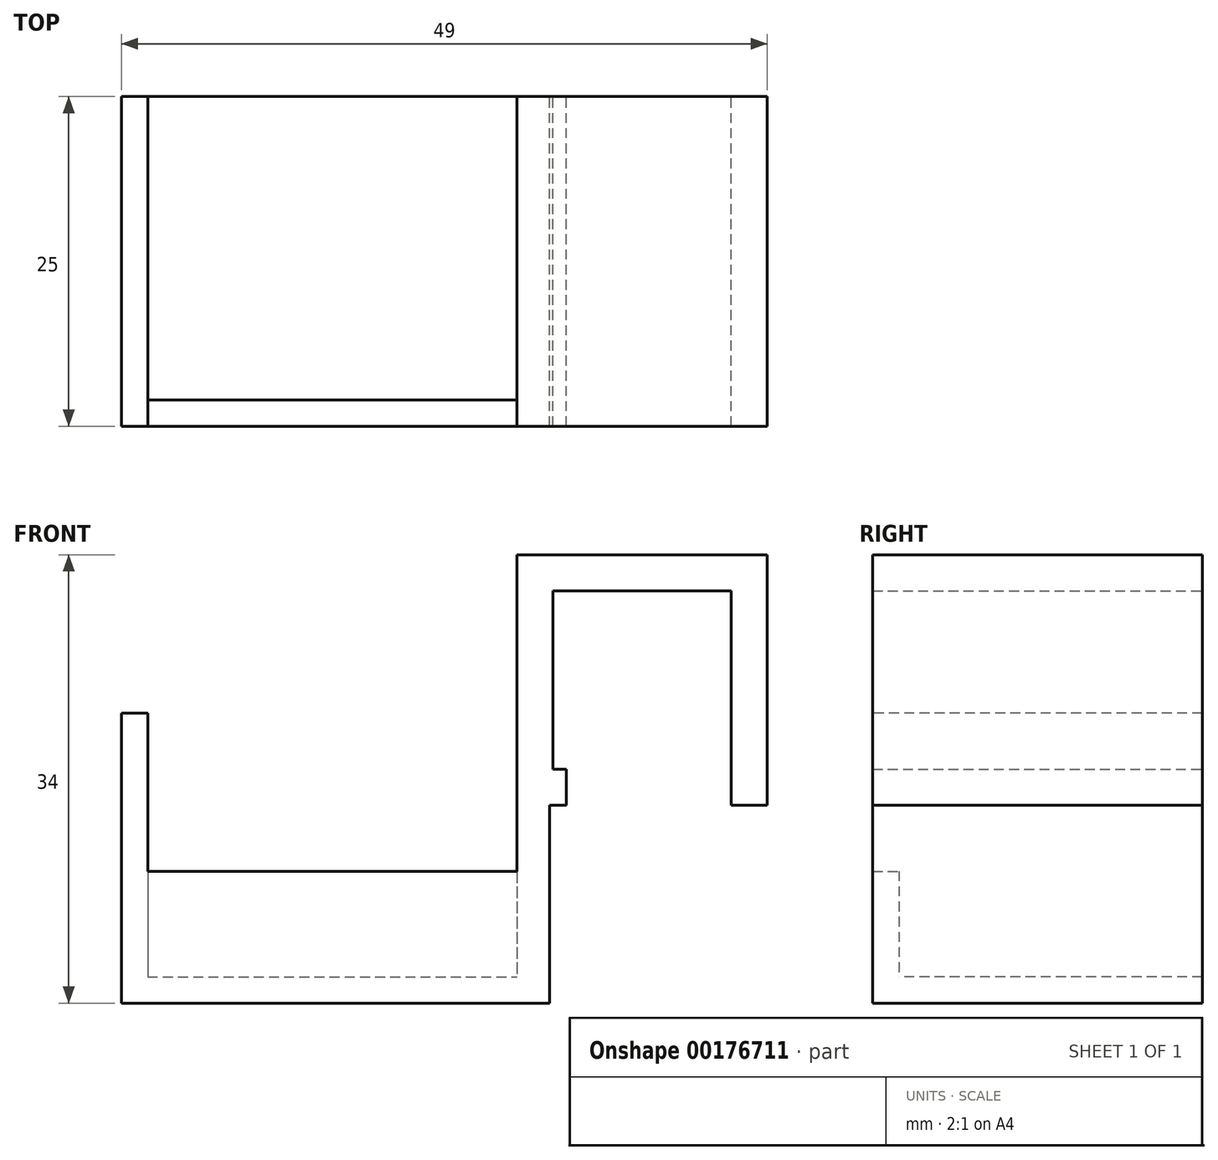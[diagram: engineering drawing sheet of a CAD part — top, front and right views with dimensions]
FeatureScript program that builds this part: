
annotation { "Feature Type Name" : "Feature", "Feature Type Description" : "" }
export const myFeature = defineFeature(function(context is Context, id is Id, definition is map)
    precondition{}
    {
        {
            var Q0;
            Q0=qCreatedBy(makeId("Front.planeOp"),FACE);
            var sketch = newSketch(context, id + "F0", { "sketchPlane" : qUnion([Q0])});
            skLineSegment(sketch, "E0.bottom", {"start": v(9.5, 9.5) * mm, "end": v(-9.5, 9.5) * mm});
            skLineSegment(sketch, "E0.top", {"start": v(9.5, -9.5) * mm, "end": v(-9.5, -9.5) * mm});
            skLineSegment(sketch, "E0.left", {"start": v(9.5, 9.5) * mm, "end": v(9.5, -9.5) * mm});
            skLineSegment(sketch, "E0.right", {"start": v(-9.5, 9.5) * mm, "end": v(-9.5, -9.5) * mm});
            skPoint(sketch, "E0.middle", {"position": v(0, 0) * mm});
            skLineSegment(sketch, "E1.bottom", {"start": v(6.75, 6.75) * mm, "end": v(-6.75, 6.75) * mm});
            skLineSegment(sketch, "E1.top", {"start": v(6.75, -6.75) * mm, "end": v(-6.75, -6.75) * mm});
            skLineSegment(sketch, "E1.left", {"start": v(6.75, 6.75) * mm, "end": v(6.75, -6.75) * mm});
            skLineSegment(sketch, "E1.right", {"start": v(-6.75, 6.75) * mm, "end": v(-6.75, -6.75) * mm});
            skLineSegment(sketch, "E2", {"start": v(-5.75, -6.75) * mm, "end": v(-5.75, -9.5) * mm});
            skLineSegment(sketch, "E3", {"start": v(-5.75, -9.5) * mm, "end": v(6.75, -9.5) * mm});
            skLineSegment(sketch, "E4", {"start": v(6.75, -9.5) * mm, "end": v(6.75, -6.75) * mm});
            skSolve(sketch);
        }
        {
            var Q0;
            Q0=makeQuery(id+"F0.imprint","IMPRINT",FACE,{"disambiguationData":[TD([[makeQuery(id+"F0.imprint","IMPRINT",EDGE,{"derivedFrom":sQuery(id+"F0.wireOp",EDGE,"E0.bottom")}),1.0]])]});
            extrude(context, id + "F1", {"entities" : qUnion([Q0]), "endBound" : BoundingType.SYMMETRIC, "depth" : 25 * mm});
        }
        {
            var Q0;
            Q0=makeQuery(id+"F1.opExtrude","SWEPT_FACE",FACE,{"disambiguationData":[OSD([sQuery(id+"F0.wireOp",EDGE,"E0.right")])]});
            var sketch = newSketch(context, id + "F2", { "sketchPlane" : qUnion([Q0])});
            skLineSegment(sketch, "E5.bottom", {"start": v(-12.5, 9.5) * mm, "end": v(12.5, 9.5) * mm});
            skLineSegment(sketch, "E5.top", {"start": v(-12.5, -24.5) * mm, "end": v(12.5, -24.5) * mm});
            skLineSegment(sketch, "E5.left", {"start": v(-12.5, 9.5) * mm, "end": v(-12.5, -24.5) * mm});
            skLineSegment(sketch, "E5.right", {"start": v(12.5, 9.5) * mm, "end": v(12.5, -24.5) * mm});
            skSolve(sketch);
        }
        {
            var Q0;
            Q0=qSketchRegion(id+"F2",true);
            extrude(context, id + "F3", {"entities" : qUnion([Q0]), "operationType" : NewBodyOperationType.ADD, "oppositeDirection" : true, "depth" : 2.5 * mm});
        }
        {
            var Q0;
            Q0=makeQuery(id+"F3.boolean.opBoolean","MERGE",FACE,{"derivedFrom":[makeQuery(id+"F1.opExtrude","SWEPT_FACE",FACE,{"disambiguationData":[OSD([sQuery(id+"F0.wireOp",EDGE,"E0.right")])]}),makeQuery(id+"F3.opExtrude","CAP_FACE",FACE,{"disambiguationData":[OSD([sQuery(id+"F2.wireOp",EDGE,"E5.bottom"),sQuery(id+"F2.wireOp",EDGE,"E5.top"),sQuery(id+"F2.wireOp",EDGE,"E5.left"),sQuery(id+"F2.wireOp",EDGE,"E5.right")])],"isStart":true})]});
            var sketch = newSketch(context, id + "F4", { "sketchPlane" : qUnion([Q0])});
            skLineSegment(sketch, "E6.bottom", {"start": v(-12.5, -24.5) * mm, "end": v(12.5, -24.5) * mm});
            skLineSegment(sketch, "E6.top", {"start": v(-12.5, -22.5) * mm, "end": v(12.5, -22.5) * mm});
            skLineSegment(sketch, "E6.left", {"start": v(-12.5, -24.5) * mm, "end": v(-12.5, -22.5) * mm});
            skLineSegment(sketch, "E6.right", {"start": v(12.5, -24.5) * mm, "end": v(12.5, -22.5) * mm});
            skSolve(sketch);
        }
        {
            var Q0;
            Q0=qSketchRegion(id+"F4",true);
            extrude(context, id + "F5", {"entities" : qUnion([Q0]), "operationType" : NewBodyOperationType.ADD, "depth" : 30 * mm});
        }
        {
            var Q0;
            Q0=makeQuery(id+"F5.opExtrude","SWEPT_FACE",FACE,{"disambiguationData":[OSD([sQuery(id+"F4.wireOp",EDGE,"E6.top")])]});
            var sketch = newSketch(context, id + "F6", { "sketchPlane" : qUnion([Q0])});
            skLineSegment(sketch, "E7.bottom", {"start": v(-39.5, 12.5) * mm, "end": v(-37.5, 12.5) * mm});
            skLineSegment(sketch, "E7.top", {"start": v(-39.5, -12.5) * mm, "end": v(-37.5, -12.5) * mm});
            skLineSegment(sketch, "E7.left", {"start": v(-39.5, 12.5) * mm, "end": v(-39.5, -12.5) * mm});
            skLineSegment(sketch, "E7.right", {"start": v(-37.5, 12.5) * mm, "end": v(-37.5, -12.5) * mm});
            skSolve(sketch);
        }
        {
            var Q0;
            Q0=qSketchRegion(id+"F6",true);
            extrude(context, id + "F7", {"entities" : qUnion([Q0]), "operationType" : NewBodyOperationType.ADD, "depth" : 20 * mm});
        }
        {
            var Q0;
            Q0=makeQuery(id+"F7.boolean.opBoolean","MERGE",FACE,{"derivedFrom":[makeQuery(id+"F5.boolean.opBoolean","MERGE",FACE,{"derivedFrom":[makeQuery(id+"F3.boolean.opBoolean","MERGE",FACE,{"derivedFrom":[makeQuery(id+"F1.opExtrude","CAP_FACE",FACE,{"disambiguationData":[OSD([sQuery(id+"F0.wireOp",EDGE,"E0.bottom"),sQuery(id+"F0.wireOp",EDGE,"E0.top"),sQuery(id+"F0.wireOp",EDGE,"E0.left"),sQuery(id+"F0.wireOp",EDGE,"E0.right"),sQuery(id+"F0.wireOp",EDGE,"E1.bottom"),sQuery(id+"F0.wireOp",EDGE,"E1.top"),sQuery(id+"F0.wireOp",EDGE,"E1.left"),sQuery(id+"F0.wireOp",EDGE,"E1.right")])],"isStart":false}),makeQuery(id+"F3.opExtrude","SWEPT_FACE",FACE,{"disambiguationData":[OSD([sQuery(id+"F2.wireOp",EDGE,"E5.right")])]})]}),makeQuery(id+"F5.opExtrude","SWEPT_FACE",FACE,{"disambiguationData":[OSD([sQuery(id+"F4.wireOp",EDGE,"E6.right")])]})]}),makeQuery(id+"F7.opExtrude","SWEPT_FACE",FACE,{"disambiguationData":[OSD([sQuery(id+"F6.wireOp",EDGE,"E7.top")])]})]});
            var sketch = newSketch(context, id + "F8", { "sketchPlane" : qUnion([Q0])});
            skLineSegment(sketch, "E8.bottom", {"start": v(-39.5, -24.5) * mm, "end": v(-7, -24.5) * mm});
            skLineSegment(sketch, "E8.top", {"start": v(-39.5, -14.5) * mm, "end": v(-7, -14.5) * mm});
            skLineSegment(sketch, "E8.left", {"start": v(-39.5, -24.5) * mm, "end": v(-39.5, -14.5) * mm});
            skLineSegment(sketch, "E8.right", {"start": v(-7, -24.5) * mm, "end": v(-7, -14.5) * mm});
            skSolve(sketch);
        }
        {
            var Q0;
            Q0=qSketchRegion(id+"F8",true);
            extrude(context, id + "F9", {"entities" : qUnion([Q0]), "operationType" : NewBodyOperationType.ADD, "oppositeDirection" : true, "depth" : 2 * mm});
        }
    });
